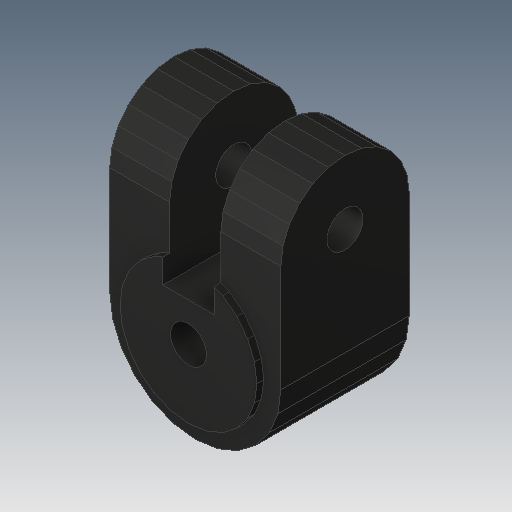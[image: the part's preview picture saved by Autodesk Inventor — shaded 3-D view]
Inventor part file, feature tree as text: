
AUTODESK INVENTOR PART (.ipt)
format: ipt  version: 2017 (Build 210142000, 142)  size: 247,808 bytes
history: native  units: mm
features: other x2, extrude x2, sketch x2
ambient origin geometry x8: Origin, YZ Plane, XZ Plane, XY Plane, X Axis, Y Axis, Z Axis, Center Point
bodies: Solid1 (feature_tree)
feature tree (6):
  other  "LCD Mount Part 2"
  other  "MeshFeature1"
  extrude  "Extrusion1"  Depth=10.0mm TaperAngle=0.0deg
  extrude  "Extrusion2"  Depth=10.0mm TaperAngle=0.0deg
  sketch  "Sketch1"  dims[d0=4.2mm d1=10.0mm d2=0.0mm]
  sketch  "Sketch2"  dims[d3=4.2mm d4=10.0mm d5=0.0mm]
